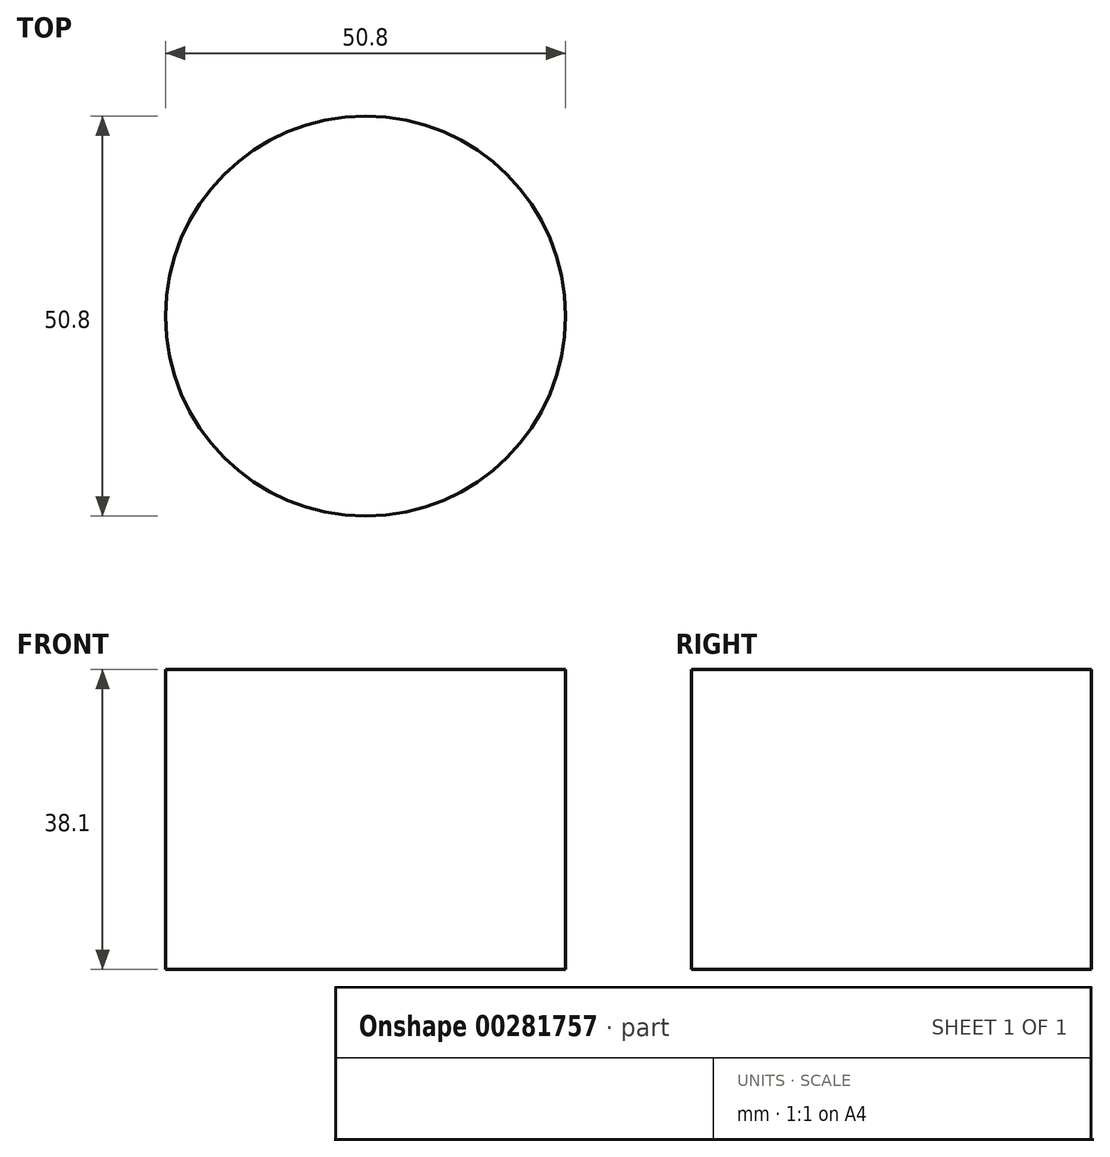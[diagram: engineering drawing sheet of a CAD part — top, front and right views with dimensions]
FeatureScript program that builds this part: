
annotation { "Feature Type Name" : "Feature", "Feature Type Description" : "" }
export const myFeature = defineFeature(function(context is Context, id is Id, definition is map)
    precondition{}
    {
        {
            var Q0;
            Q0=qCreatedBy(makeId("Top.planeOp"),FACE);
            var sketch = newSketch(context, id + "F0", { "sketchPlane" : qUnion([Q0])});
            skCircle(sketch, "E0", {"center": v(-9.93, 40) * mm, "radius": 25.4 * mm});
            skSolve(sketch);
        }
        {
            var Q0;
            Q0=makeQuery(id+"F0.imprint","IMPRINT",FACE,{"disambiguationData":[TD([[makeQuery(id+"F0.imprint","IMPRINT",EDGE,{"derivedFrom":sQuery(id+"F0.wireOp",EDGE,"E0")}),1.0]])]});
            extrude(context, id + "F1", {"entities" : qUnion([Q0]), "depth" : 38.1 * mm});
        }
    });
